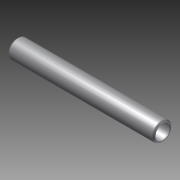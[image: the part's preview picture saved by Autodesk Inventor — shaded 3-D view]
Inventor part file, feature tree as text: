
AUTODESK INVENTOR PART (.ipt)
format: ipt  version: 2012 (Build 160160000, 160)  size: 123,904 bytes
history: native  units: in
note: dims shown in document units (in); Inventor stores cm internally (conversion verified against a paired STEP export)
features: other x42, revolve x1, sketch x1
ambient origin geometry x8: Origin, YZ Plane, XZ Plane, XY Plane, X Axis, Y Axis, Z Axis, Center Point
bodies: Solid1 (feature_tree)
feature tree (44):
  revolve  "Revolution1"  [1 undecoded]
  other  "tube_front_XY"
  other  "tube_front_YZ"
  other  "tube_front_ZX"
  other  "tube_front_X"
  other  "tube_front_Y"
  other  "tube_front_Z"
  other  "tube_front_Center"
  other  "tube_rear_XY"
  other  "tube_rear_YZ"
  other  "tube_rear_ZX"
  other  "tube_rear_X"
  other  "tube_rear_Y"
  other  "tube_rear_Z"
  other  "tube_rear_Center"
  other  "cp1_XY"
  other  "cp1_YZ"
  other  "cp1_ZX"
  other  "cp1_X"
  other  "cp1_Y"
  other  "cp1_Z"
  other  "cp1_Center"
  other  "cp2_XY"
  other  "cp2_YZ"
  other  "cp2_ZX"
  other  "cp2_X"
  other  "cp2_Y"
  other  "cp2_Z"
  other  "cp2_Center"
  other  "cp3_XY"
  other  "cp3_YZ"
  other  "cp3_ZX"
  other  "cp3_X"
  other  "cp3_Y"
  other  "cp3_Z"
  other  "cp3_Center"
  other  "cp4_XY"
  other  "cp4_YZ"
  other  "cp4_ZX"
  other  "cp4_X"
  other  "cp4_Y"
  other  "cp4_Z"
  other  "cp4_Center"
  sketch  "Sketch_1"  dims[d0=360.0deg]
note: 1 required parameter value undecoded (feature->parameter linkage not recoverable at this tier; creation-order binding heuristic only, values carry confidence <= 0.55)
